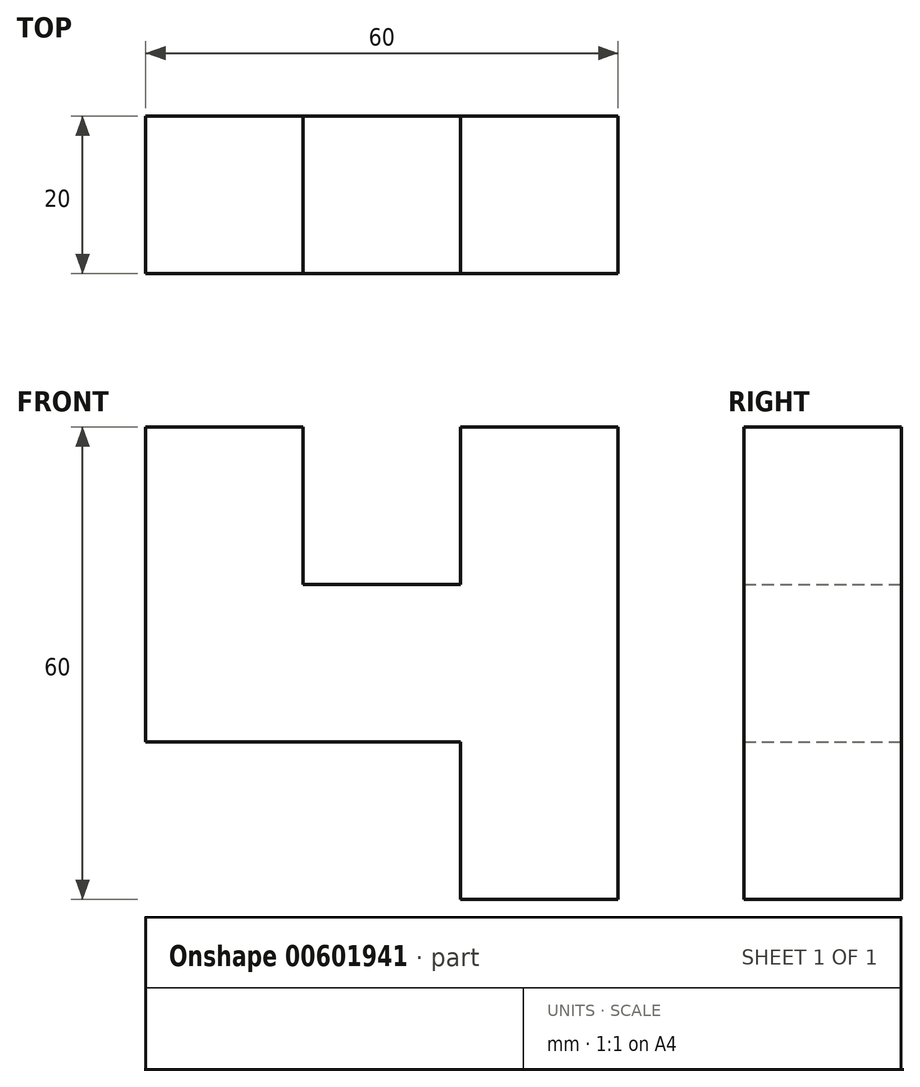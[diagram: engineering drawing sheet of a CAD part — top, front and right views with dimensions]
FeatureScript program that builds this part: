
annotation { "Feature Type Name" : "Feature", "Feature Type Description" : "" }
export const myFeature = defineFeature(function(context is Context, id is Id, definition is map)
    precondition{}
    {
        {
            var Q0;
            Q0=qCreatedBy(makeId("Front.planeOp"),FACE);
            var sketch = newSketch(context, id + "F0", { "sketchPlane" : qUnion([Q0])});
            skLineSegment(sketch, "E0", {"start": v(-51.37, 52.08) * mm, "end": v(-51.37, 12.08) * mm});
            skLineSegment(sketch, "E1", {"start": v(-51.37, 52.08) * mm, "end": v(-31.37, 52.08) * mm});
            skLineSegment(sketch, "E2", {"start": v(-31.37, 52.08) * mm, "end": v(-31.37, 32.08) * mm});
            skLineSegment(sketch, "E3", {"start": v(-31.37, 32.08) * mm, "end": v(-11.37, 32.08) * mm});
            skLineSegment(sketch, "E4", {"start": v(-11.37, 32.08) * mm, "end": v(-11.37, 52.08) * mm});
            skLineSegment(sketch, "E5", {"start": v(-11.37, 52.08) * mm, "end": v(8.63, 52.08) * mm});
            skLineSegment(sketch, "E6", {"start": v(8.63, 52.08) * mm, "end": v(8.63, -7.92) * mm});
            skLineSegment(sketch, "E7", {"start": v(8.63, -7.92) * mm, "end": v(-11.37, -7.92) * mm});
            skLineSegment(sketch, "E8", {"start": v(-11.37, -7.92) * mm, "end": v(-11.37, 12.08) * mm});
            skLineSegment(sketch, "E9", {"start": v(-11.37, 12.08) * mm, "end": v(-51.37, 12.08) * mm});
            skSolve(sketch);
        }
        {
            var Q0;
            Q0 = qSketchRegion(id + "F0", true);
            extrude(context, id + "F1", {"entities" : qUnion([Q0]), "depth" : 20 * mm, "offsetDistance" : 25 * mm});
        }
    });
